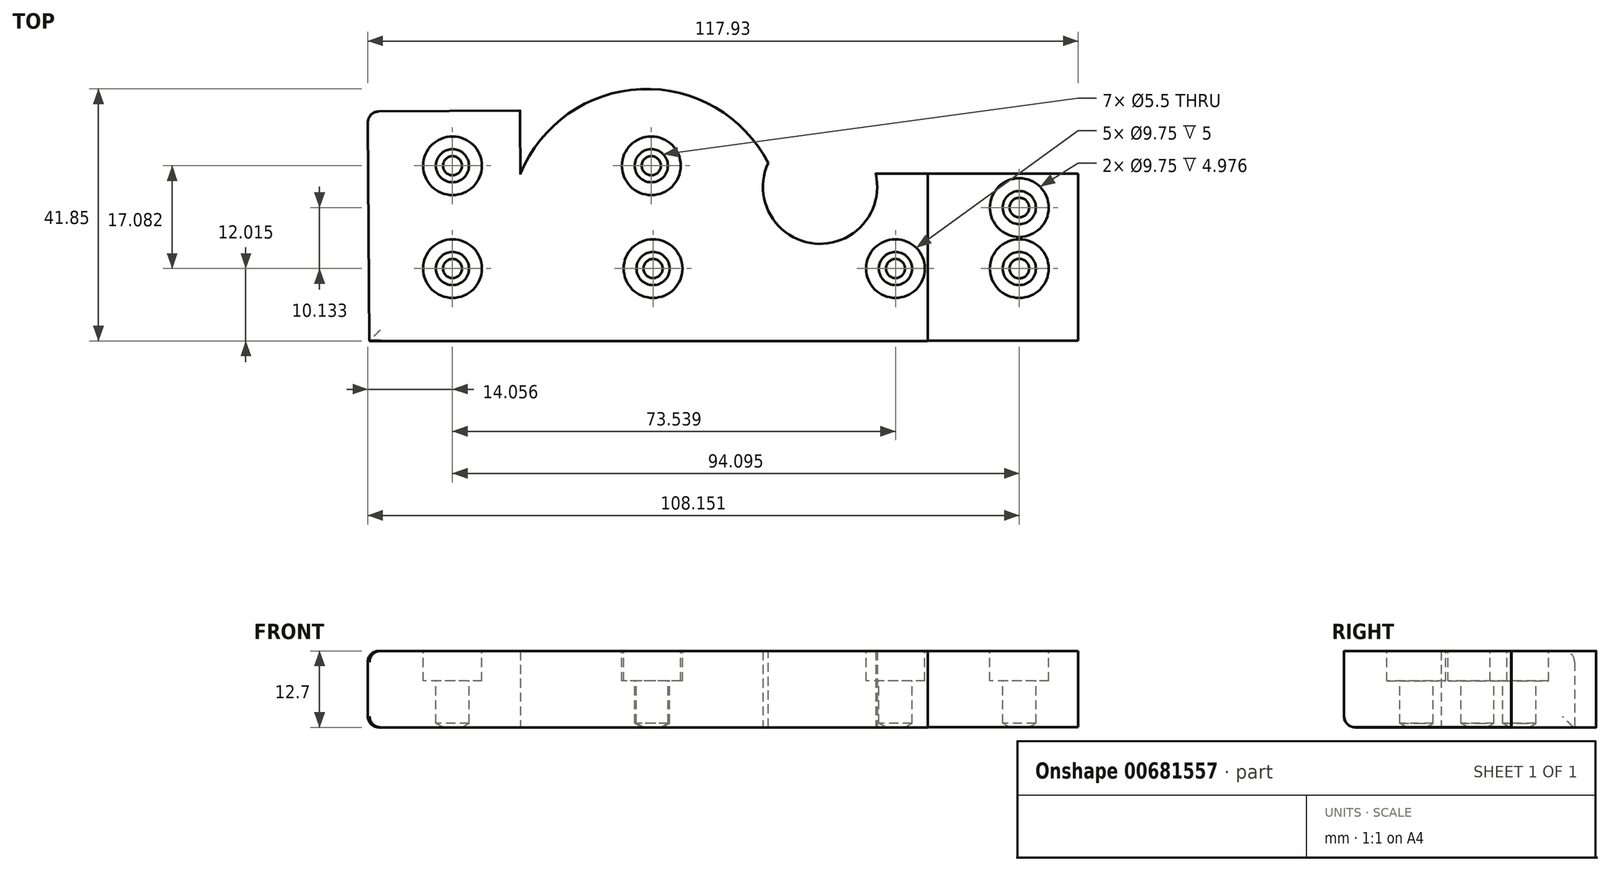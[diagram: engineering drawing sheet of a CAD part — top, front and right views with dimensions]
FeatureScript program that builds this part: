
annotation { "Feature Type Name" : "Feature", "Feature Type Description" : "" }
export const myFeature = defineFeature(function(context is Context, id is Id, definition is map)
    precondition{}
    {
        {
            var Q0;
            Q0=qCreatedBy(makeId("Top.planeOp"),FACE);
            var sketch = newSketch(context, id + "F0", { "sketchPlane" : qUnion([Q0])});
            skLineSegment(sketch, "E0", {"start": v(-66.18, 0) * mm, "end": v(-66.48, 38.1) * mm});
            skLineSegment(sketch, "E1", {"start": v(-66.48, 38.1) * mm, "end": v(-41.18, 38.29) * mm});
            skLineSegment(sketch, "E2", {"start": v(-41.18, 38.29) * mm, "end": v(-41.1, 27.8) * mm});
            skArc(sketch, "E3", {"start": v(0, 29.56) * mm, "mid": v(-21.11, 41.83) * mm, "end": v(-41.1, 27.8) * mm});
            skArc(sketch, "E4", {"start": v(0, 29.56) * mm, "mid": v(7.69, 16.16) * mm, "end": v(17.85, 27.8) * mm});
            skLineSegment(sketch, "E5.bottom", {"start": v(17.85, 27.8) * mm, "end": v(26.47, 27.8) * mm});
            skLineSegment(sketch, "E5.left", {"start": v(17.85, 27.8) * mm, "end": v(17.85, 37.8) * mm});
            skLineSegment(sketch, "E5.right", {"start": v(26.47, 27.8) * mm, "end": v(26.47, 34.86) * mm});
            skLineSegment(sketch, "E6", {"start": v(17.85, 37.8) * mm, "end": v(26.47, 34.86) * mm});
            skLineSegment(sketch, "E7", {"start": v(26.47, 27.8) * mm, "end": v(26.47, 0) * mm});
            skLineSegment(sketch, "E8", {"start": v(26.47, 0) * mm, "end": v(-66.18, 0) * mm});
            skSolve(sketch);
        }
        {
            var Q0;
            Q0=makeQuery(id+"F0.imprint","IMPRINT",FACE,{"disambiguationData":[TD([[makeQuery(id+"F0.imprint","IMPRINT",EDGE,{"derivedFrom":sQuery(id+"F0.wireOp",EDGE,"E0")}),-1.0]])]});
            extrude(context, id + "F1", {"entities" : qUnion([Q0]), "depth" : 12.7 * mm, "offsetDistance" : 25.4 * mm});
        }
        {
            var Q0;
            Q0=makeQuery(id+"F1.opExtrude","CAP_EDGE",EDGE,{"disambiguationData":[OSD([sQuery(id+"F0.wireOp",EDGE,"E1")])],"isStart":false});
            var Q1;
            Q1=makeQuery(id+"F1.opExtrude","CAP_EDGE",EDGE,{"disambiguationData":[OSD([sQuery(id+"F0.wireOp",EDGE,"E0")])],"isStart":false});
            var Q2;
            Q2=makeQuery(id+"F1.opExtrude","CAP_EDGE",EDGE,{"disambiguationData":[OSD([sQuery(id+"F0.wireOp",EDGE,"E8")])],"isStart":true});
            var Q3;
            Q3=makeQuery(id+"F1.opExtrude","CAP_EDGE",EDGE,{"disambiguationData":[OSD([sQuery(id+"F0.wireOp",EDGE,"E0")])],"isStart":true});
            var Q4;
            Q4=makeQuery(id+"F1.opExtrude","SWEPT_EDGE",EDGE,{"disambiguationData":[OSD([sQuery(id+"F0.wireOp",EDGE,"E0"),sQuery(id+"F0.wireOp",EDGE,"E1")])]});
            fillet(context, id + "F2", {"entities" : qUnion([Q0, Q1, Q2, Q3, Q4]), "radius" : 1.84 * mm, "tangentPropagation" : true, "allowEdgeOverflow" : false});
        }
        {
            var Q0;
            Q0=makeQuery(id+"F1.opExtrude","SWEPT_EDGE",EDGE,{"disambiguationData":[OSD([sQuery(id+"F0.wireOp",EDGE,"E5.bottom"),sQuery(id+"F0.wireOp",EDGE,"E5.right"),sQuery(id+"F0.wireOp",EDGE,"E7")])]});
            var Q1;
            Q1=makeQuery(id+"F1.opExtrude","SWEPT_EDGE",EDGE,{"disambiguationData":[OSD([sQuery(id+"F0.wireOp",EDGE,"E4"),sQuery(id+"F0.wireOp",EDGE,"E5.bottom"),sQuery(id+"F0.wireOp",EDGE,"E5.left")])]});
            var Q2;
            Q2=makeQuery(id+"F1.opExtrude","SWEPT_EDGE",EDGE,{"disambiguationData":[OSD([sQuery(id+"F0.wireOp",EDGE,"E3"),sQuery(id+"F0.wireOp",EDGE,"E4")])]});
            var Q3;
            Q3=makeQuery(id+"F1.opExtrude","CAP_EDGE",EDGE,{"disambiguationData":[OSD([sQuery(id+"F0.wireOp",EDGE,"E3")])],"isStart":false});
            var Q4;
            Q4=makeQuery(id+"F1.opExtrude","CAP_FACE",FACE,{"disambiguationData":[OSD([sQuery(id+"F0.wireOp",EDGE,"E0"),sQuery(id+"F0.wireOp",EDGE,"E1"),sQuery(id+"F0.wireOp",EDGE,"E2"),sQuery(id+"F0.wireOp",EDGE,"E3"),sQuery(id+"F0.wireOp",EDGE,"E4"),sQuery(id+"F0.wireOp",EDGE,"E5.bottom"),sQuery(id+"F0.wireOp",EDGE,"E7"),sQuery(id+"F0.wireOp",EDGE,"E8")])],"isStart":false});
            var Q5;
            Q5=makeQuery(id+"F1.opExtrude","CAP_EDGE",EDGE,{"disambiguationData":[OSD([sQuery(id+"F0.wireOp",EDGE,"E3")])],"isStart":true});
            var Q6;
            Q6=makeQuery(id+"F1.opExtrude","CAP_EDGE",EDGE,{"disambiguationData":[OSD([sQuery(id+"F0.wireOp",EDGE,"E1")])],"isStart":true});
            var Q7;
            Q7=makeQuery(id+"F1.opExtrude","CAP_FACE",FACE,{"disambiguationData":[OSD([sQuery(id+"F0.wireOp",EDGE,"E0"),sQuery(id+"F0.wireOp",EDGE,"E1"),sQuery(id+"F0.wireOp",EDGE,"E2"),sQuery(id+"F0.wireOp",EDGE,"E3"),sQuery(id+"F0.wireOp",EDGE,"E4"),sQuery(id+"F0.wireOp",EDGE,"E5.bottom"),sQuery(id+"F0.wireOp",EDGE,"E7"),sQuery(id+"F0.wireOp",EDGE,"E8")])],"isStart":true});
            var Q8;
            Q8=makeQuery(id+"F1.opExtrude","CAP_EDGE",EDGE,{"disambiguationData":[OSD([sQuery(id+"F0.wireOp",EDGE,"E7")])],"isStart":false});
            fillet(context, id + "F3", {"entities" : qUnion([Q0, Q1, Q2, Q3, Q4, Q5, Q6, Q7, Q8]), "radius" : 0.02 * mm, "tangentPropagation" : true, "allowEdgeOverflow" : false});
        }
        {
            var Q0;
            Q0=makeQuery(id+"F1.opExtrude","SWEPT_FACE",FACE,{"disambiguationData":[OSD([sQuery(id+"F0.wireOp",EDGE,"E7")])]});
            extrude(context, id + "F4", {"entities" : qUnion([Q0]), "operationType" : NewBodyOperationType.ADD, "depth" : 25 * mm, "offsetDistance" : 25 * mm});
        }
        {
            var Q0;
            Q0=makeQuery(id+"F1.opExtrude","CAP_FACE",FACE,{"disambiguationData":[OSD([sQuery(id+"F0.wireOp",EDGE,"E0"),sQuery(id+"F0.wireOp",EDGE,"E1"),sQuery(id+"F0.wireOp",EDGE,"E2"),sQuery(id+"F0.wireOp",EDGE,"E3"),sQuery(id+"F0.wireOp",EDGE,"E4"),sQuery(id+"F0.wireOp",EDGE,"E5.bottom"),sQuery(id+"F0.wireOp",EDGE,"E7"),sQuery(id+"F0.wireOp",EDGE,"E8")])],"isStart":false});
            var sketch = newSketch(context, id + "F5", { "sketchPlane" : qUnion([Q0])});
            skPoint(sketch, "E9", {"position": v(-52.4, 29.1) * mm});
            skPoint(sketch, "E10", {"position": v(-52.4, 12.02) * mm});
            skPoint(sketch, "E11", {"position": v(-19.1, 12.02) * mm});
            skPoint(sketch, "E12", {"position": v(-19.4, 29.1) * mm});
            skPoint(sketch, "E13", {"position": v(21.14, 12.02) * mm});
            skPoint(sketch, "E14", {"position": v(41.7, 12.02) * mm});
            skPoint(sketch, "E15", {"position": v(41.7, 22.15) * mm});
            skSolve(sketch);
        }
        {
            var Q0;
            Q0=sQuery(id+"F5.wireOp",VERTEX,"E9");
            var Q1;
            Q1=sQuery(id+"F5.wireOp",VERTEX,"E10");
            var Q2;
            Q2=sQuery(id+"F5.wireOp",VERTEX,"E11");
            var Q3;
            Q3=sQuery(id+"F5.wireOp",VERTEX,"E12");
            var Q4;
            Q4=sQuery(id+"F5.wireOp",VERTEX,"E13");
            var Q5;
            Q5=sQuery(id+"F5.wireOp",VERTEX,"E14");
            var Q6;
            Q6=sQuery(id+"F5.wireOp",VERTEX,"E15");
            var Q7;
            Q7=makeQuery(id+"F1.opExtrude","SWEPT_BODY",BODY,{"disambiguationData":[OSD([sQuery(id+"F0.wireOp",EDGE,"E0"),sQuery(id+"F0.wireOp",EDGE,"E1"),sQuery(id+"F0.wireOp",EDGE,"E2"),sQuery(id+"F0.wireOp",EDGE,"E3"),sQuery(id+"F0.wireOp",EDGE,"E4"),sQuery(id+"F0.wireOp",EDGE,"E5.bottom"),sQuery(id+"F0.wireOp",EDGE,"E7"),sQuery(id+"F0.wireOp",EDGE,"E8")])]});
            hole(context, id + "F6", {"style" : HoleStyle.C_BORE, "endStyle" : HoleEndStyle.BLIND, "standardTappedOrClearance" : lookupTablePath({ "standard" : "ISO", "fit" : "Normal", "size" : "M5", "type" : "Clearance" }), "standardBlindInLast" : lookupTablePath({ "fit" : "Standard", "standard" : "ISO", "size" : "M5", "type" : "Clearance" }), "holeDiameter" : 5.5 * mm, "cBoreDiameter" : 9.75 * mm, "cBoreDepth" : 5 * mm, "majorDiameter" : 5 * mm, "holeDepth" : 12 * mm, "isTappedThrough" : true, "tappedDepth" : 12 * mm, "tapClearance" : 3, "startFromSketch" : true, "locations" : qUnion([Q0, Q1, Q2, Q3, Q4, Q5, Q6]), "scope" : qUnion([Q7])});
        }
    });
